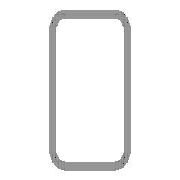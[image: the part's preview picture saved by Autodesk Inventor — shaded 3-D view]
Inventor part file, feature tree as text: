
AUTODESK INVENTOR PART (.ipt)
format: ipt  version: 2025 (Build 290162010, 162A)  size: 150,016 bytes
history: native  units: mm (DEFAULTED — no unit token found)
features: other x4, plane x3, split x2, sketch x1
ambient origin geometry x8: Origin, YZ Plane, XZ Plane, XY Plane, X Axis, Y Axis, Z Axis, Center Point
bodies: Solid1 (feature_tree), Body (feature_tree)
feature tree (10):
  parser-record x1  (decoder bookkeeping rows leaked as tree rows — omitted from the tree; the rows remain in map.json)
  other  "Driven Length"
  other  "Start Plane"
  other  "End Plane"
  plane  "Work Plane4"
  split  "Split1"
  plane  "Work Plane5"
  split  "Split2"
  sketch  "Sketch3"  dims[d3=1791.079259mm d4=0.0mm d7=4.0mm d9=40.0mm d11=80.0mm d12=2.0mm d13=124.457906mm d14=1915.537165mm d15=20.0mm d16=40.0mm d17=90.0deg d18=1791.079259mm]
  plane  "Work Plane3"
